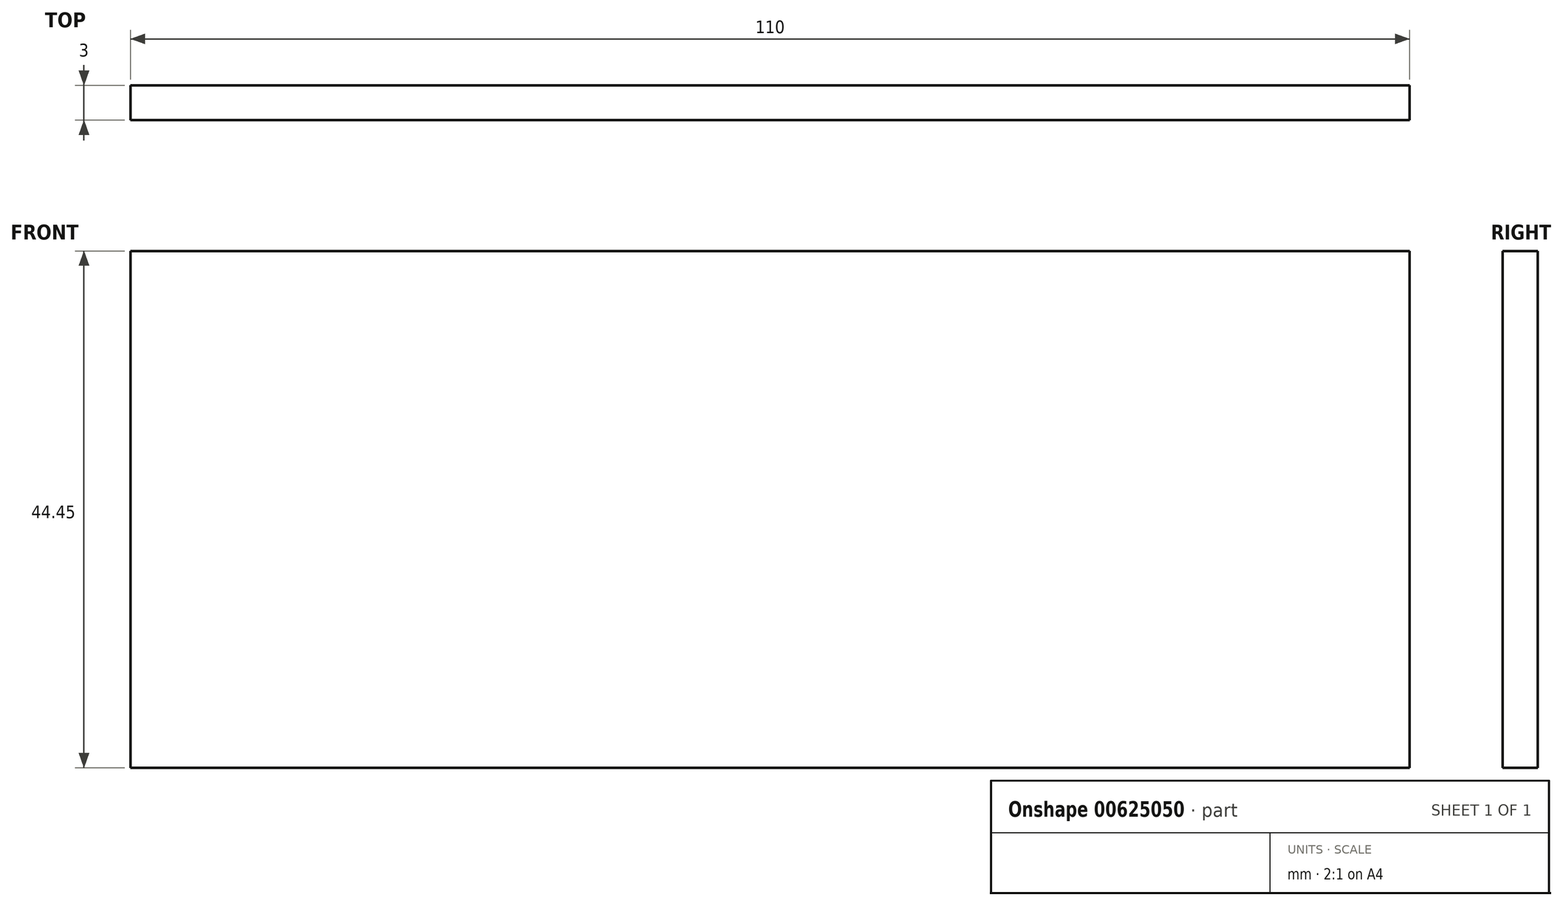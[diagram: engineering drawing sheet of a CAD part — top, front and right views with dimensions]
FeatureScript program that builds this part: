
annotation { "Feature Type Name" : "Feature", "Feature Type Description" : "" }
export const myFeature = defineFeature(function(context is Context, id is Id, definition is map)
    precondition{}
    {
        {
            var Q0;
            Q0=qCreatedBy(makeId("Front.planeOp"),FACE);
            var sketch = newSketch(context, id + "F0", { "sketchPlane" : qUnion([Q0])});
            skLineSegment(sketch, "E0.bottom", {"start": v(-66.05, 44.45) * mm, "end": v(43.95, 44.45) * mm});
            skLineSegment(sketch, "E0.top", {"start": v(-66.05, 0) * mm, "end": v(43.95, 0) * mm});
            skLineSegment(sketch, "E0.left", {"start": v(-66.05, 44.45) * mm, "end": v(-66.05, 0) * mm});
            skLineSegment(sketch, "E0.right", {"start": v(43.95, 44.45) * mm, "end": v(43.95, 0) * mm});
            skSolve(sketch);
        }
        {
            var Q0;
            Q0=makeQuery(id+"F0.imprint","IMPRINT",FACE,{"disambiguationData":[TD([[makeQuery(id+"F0.imprint","IMPRINT",EDGE,{"derivedFrom":sQuery(id+"F0.wireOp",EDGE,"E0.bottom")}),-1.0]])]});
            extrude(context, id + "F1", {"entities" : qUnion([Q0]), "depth" : 3 * mm, "offsetDistance" : 25 * mm});
        }
    });
